# Revit family: Walk_in_Door-ELT_Custom_Coolers-Single_Slide-Left_Hand
name_source: partatom
category: Doors
units: mm (PartAtom-declared; Revit-internal decimal feet)

## family parameters
Always vertical = Yes
Classification Number = 23.30.10.00
Cut with Voids When Loaded = No
Host = Wall
Room Calculation Point = No
Shared = No

## types (4) — shared parameters
Analytic Construction = <None>
Define Thermal Properties by = Schematic Type
Frame Material = ELT_Stainless Steel
Frame Thickness = 1 1/2"
Frame Width = 5 1/2"
Function = Interior
Height = 84"
Manufacturer = ELT Custom Coolers
Panel Material = ELT_White Stucco Embossed
Product Page URL = https://eltcoolerdoors.com
Rough Height = 85"
Thickness = 4"
URL = https://eltcoolerdoors.com
Wall Closure = By host

## per-type parameters (varying)
| type | Description | Door Track Length | Model | Rough Width | Width |
| 47" x 84" Cooler, Jamb Frame | Walk in Cooler Sliding Door 47” x 84“ Prehung with Jamb Frame and Header for New Construction. Left Hand | 100 1/4" | ELT 47" x 84" | 47" | 47" |
| 60" x 84" Cooler, Jamb Frame | Walk in Cooler Sliding Door 60” x 84“ Prehung with Jamb Frame and Header for New Construction. Left Hand | 126 1/4" | ELT 60" x 84" | 59" | 60" |
| 60" x 84" Freezer, Jamb Frame | Walk in Freezer Sliding Door 60” x 84“ Prehung with Jamb Frame and Header for New Construction. Left Hand | 126 1/4" | ELT 60" x 84" | 59" | 60" |
| 47" x 84" Freezer, Jamb Frame | Walk in Freezer Sliding Door 47” x 84“ Prehung with Jamb Frame and Header for New Construction. Left Hand | 100 1/4" | ELT 47" x 84" | 47" | 47" |

## geometry (parser evidence)
native form markers: Sweep x13
no freeform markers — native parametric forms only
